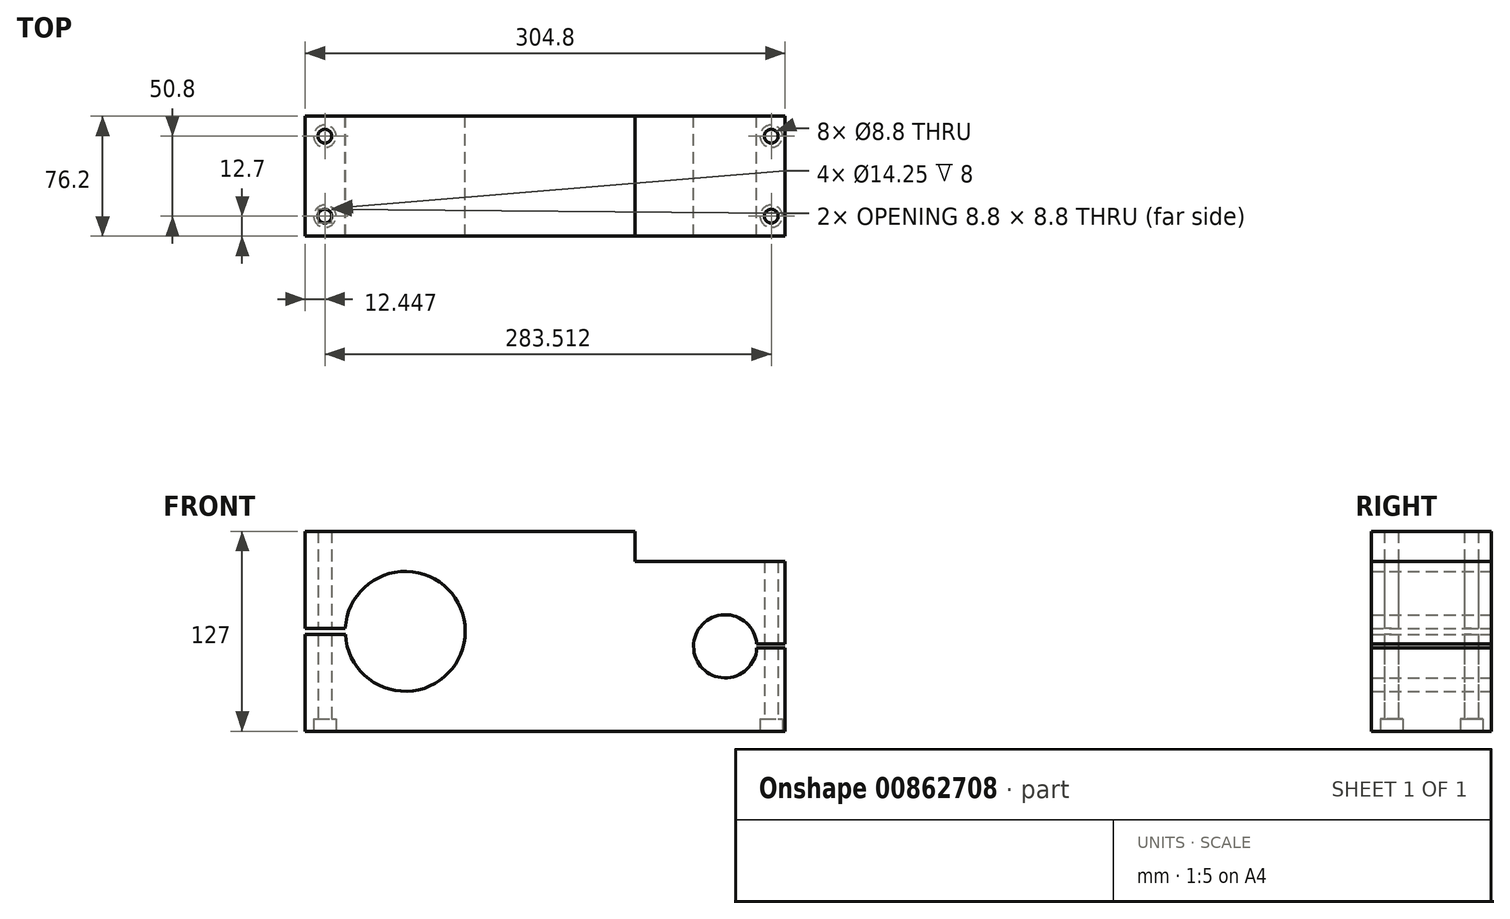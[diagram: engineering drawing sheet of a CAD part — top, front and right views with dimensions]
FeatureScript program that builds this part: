
annotation { "Feature Type Name" : "Feature", "Feature Type Description" : "" }
export const myFeature = defineFeature(function(context is Context, id is Id, definition is map)
    precondition{}
    {
        {
            var Q0;
            Q0=qCreatedBy(makeId("Front.planeOp"),FACE);
            var sketch = newSketch(context, id + "F0", { "sketchPlane" : qUnion([Q0])});
            skLineSegment(sketch, "E0", {"start": v(-167.1, 73.39) * mm, "end": v(-167.1, 11.75) * mm});
            skLineSegment(sketch, "E1", {"start": v(-167.1, -53.61) * mm, "end": v(137.7, -53.61) * mm});
            skLineSegment(sketch, "E2", {"start": v(137.7, -53.61) * mm, "end": v(137.7, -0.77) * mm});
            skLineSegment(sketch, "E3", {"start": v(137.7, 54.34) * mm, "end": v(42.46, 54.34) * mm});
            skLineSegment(sketch, "E4", {"start": v(42.46, 54.34) * mm, "end": v(42.46, 73.39) * mm});
            skLineSegment(sketch, "E5", {"start": v(42.46, 73.39) * mm, "end": v(-167.1, 73.39) * mm});
            skLineSegment(sketch, "E6", {"start": v(-103.6, 73.39) * mm, "end": v(-103.6, 47.99) * mm});
            skLineSegment(sketch, "E7", {"start": v(99.6, 54.34) * mm, "end": v(99.6, 20.43) * mm});
            skPoint(sketch, "E8", {"position": v(-103.6, 9.89) * mm});
            skPoint(sketch, "E9", {"position": v(99.6, 0.36) * mm});
            skArc(sketch, "E10", {"start": v(-141.64, 7.86) * mm, "mid": v(-65.5, 9.98) * mm, "end": v(-141.65, 11.75) * mm});
            skArc(sketch, "E11", {"start": v(119.62, 1.74) * mm, "mid": v(79.54, 0.24) * mm, "end": v(119.64, -0.77) * mm});
            skLineSegment(sketch, "E12", {"start": v(137.7, 1.74) * mm, "end": v(137.7, 54.34) * mm});
            skLineSegment(sketch, "E13", {"start": v(137.7, 1.74) * mm, "end": v(119.62, 1.74) * mm});
            skLineSegment(sketch, "E14", {"start": v(137.7, -0.77) * mm, "end": v(119.64, -0.77) * mm});
            skLineSegment(sketch, "E15", {"start": v(-167.1, 7.86) * mm, "end": v(-141.64, 7.86) * mm});
            skLineSegment(sketch, "E16", {"start": v(-167.1, 11.75) * mm, "end": v(-141.65, 11.75) * mm});
            skLineSegment(sketch, "E17.trimOffspring", {"start": v(-167.1, 7.86) * mm, "end": v(-167.1, -53.61) * mm});
            skLineSegment(sketch, "E18.trimOffspring", {"start": v(-103.6, -28.21) * mm, "end": v(-103.6, -53.61) * mm});
            skLineSegment(sketch, "E19.trimOffspring", {"start": v(99.6, -19.7) * mm, "end": v(99.6, -53.61) * mm});
            skLineSegment(sketch, "E20.trimOffspring", {"start": v(79.54, 0.36) * mm, "end": v(49.9, 0.36) * mm});
            skPoint(sketch, "E21.orphan", {"position": v(137.7, 0.36) * mm});
            skSolve(sketch);
        }
        {
            var Q0;
            Q0 = qSketchRegion(id + "F0", true);
            extrude(context, id + "F1", {"entities" : qUnion([Q0]), "depth" : 76.2 * mm, "offsetDistance" : 25.4 * mm});
        }
        {
            var Q0;
            Q0=makeQuery(id+"F1.opExtrude","SWEPT_FACE",FACE,{"disambiguationData":[OSD([sQuery(id+"F0.wireOp",EDGE,"E1")])]});
            var sketch = newSketch(context, id + "F2", { "sketchPlane" : qUnion([Q0])});
            skLineSegment(sketch, "E22", {"start": v(-154.64, 76.2) * mm, "end": v(-154.64, 0) * mm});
            skLineSegment(sketch, "E23", {"start": v(128.87, 76.2) * mm, "end": v(128.87, 0) * mm});
            skLineSegment(sketch, "E24", {"start": v(-167.1, 63.5) * mm, "end": v(137.7, 63.5) * mm});
            skLineSegment(sketch, "E25", {"start": v(-167.1, 12.7) * mm, "end": v(137.7, 12.7) * mm});
            skPoint(sketch, "E26", {"position": v(-154.64, 63.5) * mm});
            skPoint(sketch, "E27", {"position": v(-154.64, 12.7) * mm});
            skPoint(sketch, "E28", {"position": v(128.87, 12.7) * mm});
            skPoint(sketch, "E29", {"position": v(128.87, 63.5) * mm});
            skSolve(sketch);
        }
        {
            var Q0;
            Q0=sQuery(id+"F2.wireOp",VERTEX,"E26");
            var Q1;
            Q1=sQuery(id+"F2.wireOp",VERTEX,"E29");
            var Q2;
            Q2=sQuery(id+"F2.wireOp",VERTEX,"E28");
            var Q3;
            Q3=sQuery(id+"F2.wireOp",VERTEX,"E27");
            var Q4;
            Q4=makeQuery(id+"F1.opExtrude","SWEPT_BODY",BODY,{"disambiguationData":[OSD([sQuery(id+"F0.wireOp",EDGE,"E0"),sQuery(id+"F0.wireOp",EDGE,"E1"),sQuery(id+"F0.wireOp",EDGE,"E2"),sQuery(id+"F0.wireOp",EDGE,"E3"),sQuery(id+"F0.wireOp",EDGE,"E4"),sQuery(id+"F0.wireOp",EDGE,"E5"),sQuery(id+"F0.wireOp",EDGE,"E10"),sQuery(id+"F0.wireOp",EDGE,"E11"),sQuery(id+"F0.wireOp",EDGE,"E12"),sQuery(id+"F0.wireOp",EDGE,"E13"),sQuery(id+"F0.wireOp",EDGE,"E14"),sQuery(id+"F0.wireOp",EDGE,"E15"),sQuery(id+"F0.wireOp",EDGE,"E16"),sQuery(id+"F0.wireOp",EDGE,"E17.trimOffspring")])]});
            hole(context, id + "F3", {"style" : HoleStyle.C_BORE, "endStyle" : HoleEndStyle.THROUGH, "standardTappedOrClearance" : lookupTablePath({ "fit" : "Normal", "standard" : "ISO", "size" : "M8", "type" : "Clearance" }), "standardBlindInLast" : lookupTablePath({ "fit" : "Standard", "standard" : "ISO", "size" : "M8", "type" : "Clearance" }), "holeDiameter" : 8.8 * mm, "cBoreDiameter" : 14.25 * mm, "cBoreDepth" : 8 * mm, "majorDiameter" : 6.35 * mm, "isTappedThrough" : true, "tappedDepth" : 12.7 * mm, "tapClearance" : 3, "locations" : qUnion([Q0, Q1, Q2, Q3]), "scope" : qUnion([Q4])});
        }
    });
